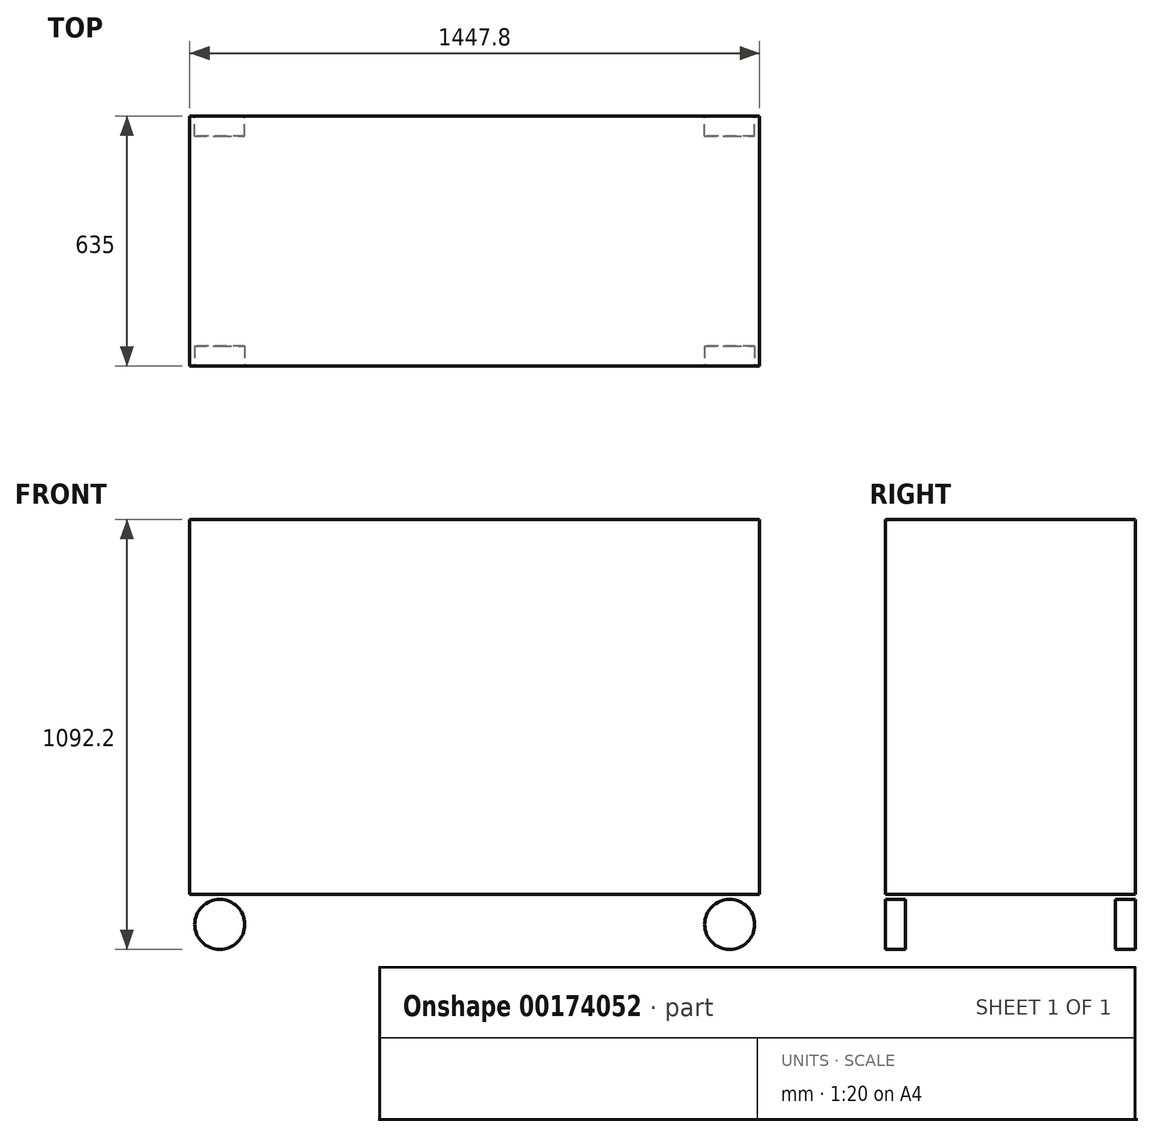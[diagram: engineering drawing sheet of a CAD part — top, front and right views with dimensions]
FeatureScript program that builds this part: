
annotation { "Feature Type Name" : "Feature", "Feature Type Description" : "" }
export const myFeature = defineFeature(function(context is Context, id is Id, definition is map)
    precondition{}
    {
        {
            var Q0;
            Q0=qCreatedBy(makeId("Front.planeOp"),FACE);
            var sketch = newSketch(context, id + "F0", { "sketchPlane" : qUnion([Q0])});
            skLineSegment(sketch, "E0.bottom", {"start": v(-723.9, 0) * mm, "end": v(723.9, 0) * mm});
            skLineSegment(sketch, "E0.top", {"start": v(-723.9, 952.5) * mm, "end": v(723.9, 952.5) * mm});
            skLineSegment(sketch, "E0.left", {"start": v(-723.9, 0) * mm, "end": v(-723.9, 952.5) * mm});
            skLineSegment(sketch, "E0.right", {"start": v(723.9, 0) * mm, "end": v(723.9, 952.5) * mm});
            skCircle(sketch, "E1", {"center": v(-647.7, -76.2) * mm, "radius": 63.5 * mm});
            skCircle(sketch, "E2", {"center": v(647.7, -76.2) * mm, "radius": 63.5 * mm});
            skSolve(sketch);
        }
        {
            var Q0;
            Q0=makeQuery(id+"F0.imprint","IMPRINT",FACE,{"disambiguationData":[TD([[makeQuery(id+"F0.imprint","IMPRINT",EDGE,{"derivedFrom":sQuery(id+"F0.wireOp",EDGE,"E0.bottom")}),1.0]])]});
            extrude(context, id + "F1", {"entities" : qUnion([Q0]), "depth" : 635 * mm});
        }
        {
            var Q0;
            Q0=makeQuery(id+"F0.imprint","IMPRINT",FACE,{"disambiguationData":[TD([[makeQuery(id+"F0.imprint","IMPRINT",EDGE,{"derivedFrom":sQuery(id+"F0.wireOp",EDGE,"E2")}),1.0]])]});
            var Q1;
            Q1=makeQuery(id+"F0.imprint","IMPRINT",FACE,{"disambiguationData":[TD([[makeQuery(id+"F0.imprint","IMPRINT",EDGE,{"derivedFrom":sQuery(id+"F0.wireOp",EDGE,"E1")}),1.0]])]});
            extrude(context, id + "F2", {"entities" : qUnion([Q0, Q1]), "depth" : 50.8 * mm});
        }
        {
            var Q0;
            Q0=makeQuery(id+"F1.opExtrude","SWEPT_EDGE",EDGE,{"disambiguationData":[OSD([sQuery(id+"F0.wireOp",EDGE,"E0.bottom"),sQuery(id+"F0.wireOp",EDGE,"E0.right")])]});
            cPoint(context, id + "F3", {"entities" : qUnion([Q0]), "parameter" : 0.5});
        }
        {
            var Q0;
            Q0=qCreatedBy(makeId("Front.planeOp"),FACE);
            var Q1;
            Q1 = qCreatedBy(id + "F3" ,VERTEX);
            cPlane(context, id + "F4", {"entities" : qUnion([Q0, Q1]), "cplaneType" : CPlaneType.PLANE_POINT, "offset" : 25.4 * mm, "width" : 152.4 * mm, "height" : 152.4 * mm});
        }
        {
            var Q0;
            Q0=makeQuery(id+"F2.opExtrude","SWEPT_BODY",BODY,{"disambiguationData":[OSD([sQuery(id+"F0.wireOp",EDGE,"E2")])]});
            var Q1;
            Q1=makeQuery(id+"F2.opExtrude","SWEPT_BODY",BODY,{"disambiguationData":[OSD([sQuery(id+"F0.wireOp",EDGE,"E1")])]});
            var Q2;
            Q2=qCreatedBy(id+"F4.planeOp",FACE);
            mirror(context, id + "F5", {"entities" : qUnion([Q0, Q1]), "mirrorPlane" : qUnion([Q2])});
        }
    });
